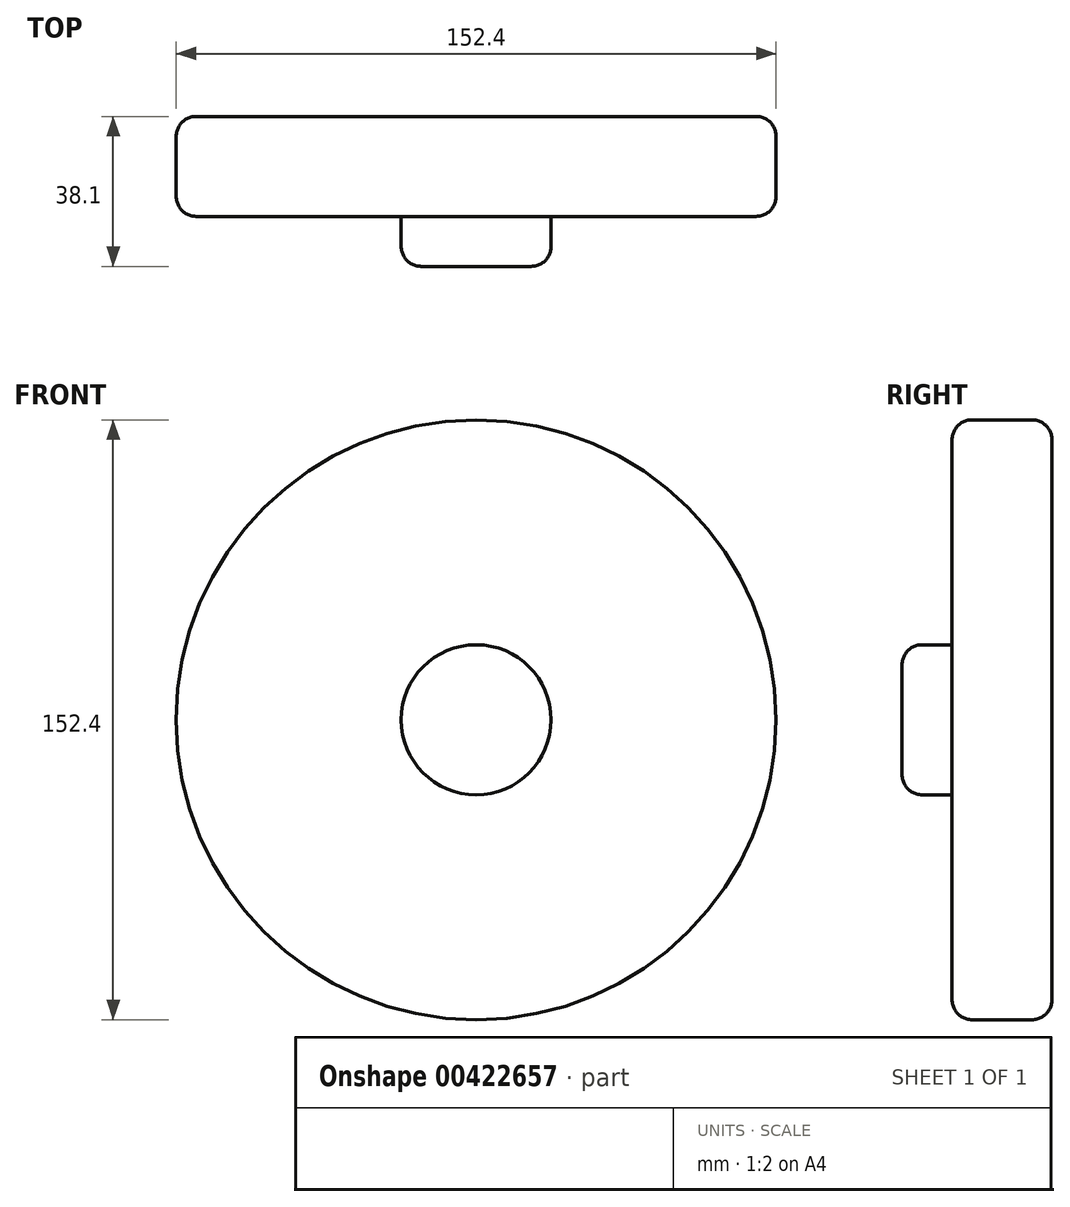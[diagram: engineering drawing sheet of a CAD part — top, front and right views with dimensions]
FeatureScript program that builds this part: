
annotation { "Feature Type Name" : "Feature", "Feature Type Description" : "" }
export const myFeature = defineFeature(function(context is Context, id is Id, definition is map)
    precondition{}
    {
        {
            var Q0;
            Q0=qCreatedBy(makeId("Front.planeOp"),FACE);
            var sketch = newSketch(context, id + "F0", { "sketchPlane" : qUnion([Q0])});
            skCircle(sketch, "E0", {"center": v(0, 0) * mm, "radius": 76.2 * mm});
            skSolve(sketch);
        }
        {
            var Q0;
            Q0=makeQuery(id+"F0.imprint","IMPRINT",FACE,{"disambiguationData":[TD([[makeQuery(id+"F0.imprint","IMPRINT",EDGE,{"derivedFrom":sQuery(id+"F0.wireOp",EDGE,"E0")}),1.0]])]});
            extrude(context, id + "F1", {"entities" : qUnion([Q0]), "depth" : 25.4 * mm});
        }
        {
            var Q0;
            Q0=makeQuery(id+"F1.opExtrude","CAP_FACE",FACE,{"disambiguationData":[OSD([sQuery(id+"F0.wireOp",EDGE,"E0")])],"isStart":false});
            var sketch = newSketch(context, id + "F2", { "sketchPlane" : qUnion([Q0])});
            skCircle(sketch, "E1", {"center": v(0, 0) * mm, "radius": 19.05 * mm});
            skSolve(sketch);
        }
        {
            var Q0;
            Q0=makeQuery(id+"F1.opExtrude","CAP_EDGE",EDGE,{"disambiguationData":[OSD([sQuery(id+"F0.wireOp",EDGE,"E0")])],"isStart":false});
            fillet(context, id + "F3", {"entities" : qUnion([Q0]), "radius" : 5.08 * mm, "tangentPropagation" : true, "allowEdgeOverflow" : false});
        }
        {
            var Q0;
            Q0=makeQuery(id+"F1.opExtrude","SWEPT_FACE",FACE,{"disambiguationData":[OSD([sQuery(id+"F0.wireOp",EDGE,"E0")])]});
            fillet(context, id + "F4", {"entities" : qUnion([Q0]), "radius" : 5.08 * mm, "tangentPropagation" : true, "allowEdgeOverflow" : false});
        }
        {
            var Q0;
            Q0=makeQuery(id+"F2.imprint","IMPRINT",FACE,{"disambiguationData":[TD([[makeQuery(id+"F2.imprint","IMPRINT",EDGE,{"derivedFrom":sQuery(id+"F2.wireOp",EDGE,"E1")}),1.0]])]});
            extrude(context, id + "F5", {"entities" : qUnion([Q0]), "operationType" : NewBodyOperationType.ADD, "depth" : 12.7 * mm, "offsetDistance" : 25.4 * mm});
        }
        {
            var Q0;
            Q0=makeQuery(id+"F5.opExtrude","CAP_EDGE",EDGE,{"disambiguationData":[OSD([sQuery(id+"F2.wireOp",EDGE,"E1")])],"isStart":false});
            fillet(context, id + "F6", {"entities" : qUnion([Q0]), "radius" : 5.08 * mm, "tangentPropagation" : true, "allowEdgeOverflow" : false});
        }
    });
